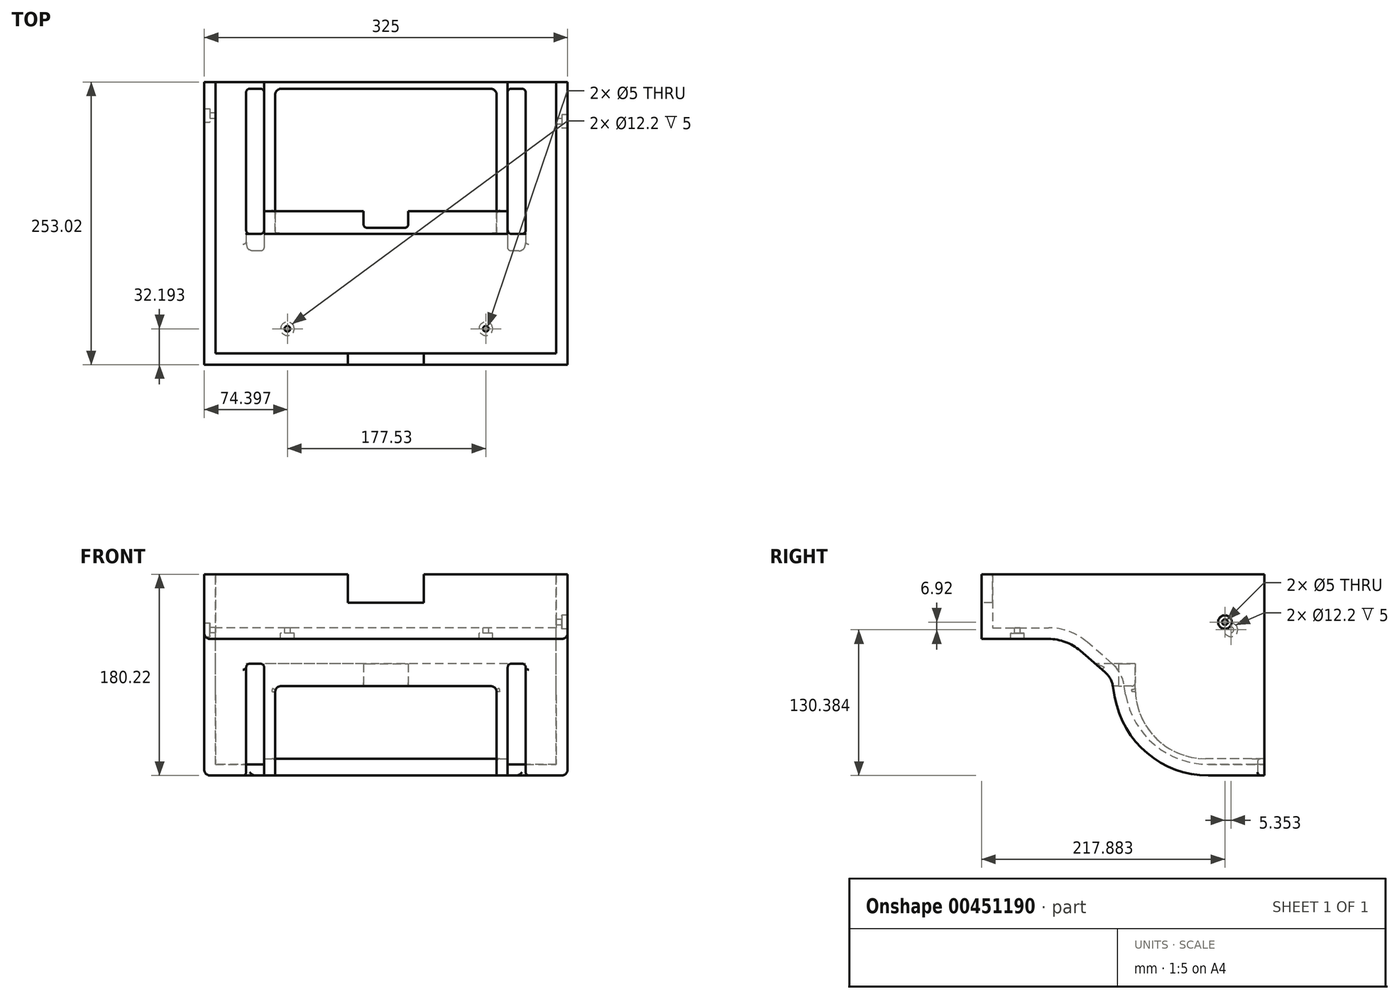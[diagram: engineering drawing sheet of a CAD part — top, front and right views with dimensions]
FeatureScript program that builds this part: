
annotation { "Feature Type Name" : "Feature", "Feature Type Description" : "" }
export const myFeature = defineFeature(function(context is Context, id is Id, definition is map)
    precondition{}
    {
        {
            var Q0;
            Q0=qCreatedBy(makeId("Right.planeOp"),FACE);
            var sketch = newSketch(context, id + "F0", { "sketchPlane" : qUnion([Q0])});
            skLineSegment(sketch, "E0", {"start": v(-253.02, 122.22) * mm, "end": v(-193.02, 122.22) * mm});
            skLineSegment(sketch, "E1", {"start": v(-50, 0) * mm, "end": v(0, 0) * mm});
            skLineSegment(sketch, "E2", {"start": v(0, 0) * mm, "end": v(0, 180.22) * mm});
            skLineSegment(sketch, "E3", {"start": v(0, 180.22) * mm, "end": v(-253.02, 180.22) * mm});
            skLineSegment(sketch, "E4", {"start": v(-253.02, 180.22) * mm, "end": v(-253.02, 122.22) * mm});
            skArc(sketch, "E5", {"start": v(-133.7, 70.24) * mm, "mid": v(-104.63, 19.89) * mm, "end": v(-50, 0) * mm});
            skLineSegment(sketch, "E6", {"start": v(-133.7, 70.24) * mm, "end": v(-135.44, 80.09) * mm});
            skPoint(sketch, "E7", {"position": v(-142.53, 92.57) * mm});
            skArc(sketch, "E8", {"start": v(-135.44, 80.09) * mm, "mid": v(-137.9, 86.94) * mm, "end": v(-142.53, 92.57) * mm});
            skLineSegment(sketch, "E9", {"start": v(-142.53, 92.57) * mm, "end": v(-164.74, 111.7) * mm});
            skArc(sketch, "E10", {"start": v(-164.74, 111.7) * mm, "mid": v(-177.94, 119.5) * mm, "end": v(-193.02, 122.22) * mm});
            skSolve(sketch);
        }
        {
            var Q0;
            Q0=qSketchRegion(id+"F0",true);
            extrude(context, id + "F1", {"entities" : qUnion([Q0]), "depth" : 325 * mm, "offsetDistance" : 25 * mm, "symmetric" : true});
        }
        {
            var Q0;
            Q0=qCreatedBy(makeId("Top.planeOp"),FACE);
            var sketch = newSketch(context, id + "F2", { "sketchPlane" : qUnion([Q0])});
            skLineSegment(sketch, "E11.bottom", {"start": v(-125, -6) * mm, "end": v(-109, -6) * mm});
            skLineSegment(sketch, "E11.top", {"start": v(-125, -161) * mm, "end": v(-109, -161) * mm});
            skLineSegment(sketch, "E11.left", {"start": v(-125, -6) * mm, "end": v(-125, -161) * mm});
            skLineSegment(sketch, "E11.right", {"start": v(-109, -6) * mm, "end": v(-109, -161) * mm});
            skLineSegment(sketch, "E12.MirrorCS", {"start": v(125, -161) * mm, "end": v(109, -161) * mm});
            skLineSegment(sketch, "E13.MirrorCS", {"start": v(125, -6) * mm, "end": v(109, -6) * mm});
            skLineSegment(sketch, "E14.MirrorCS", {"start": v(125, -6) * mm, "end": v(125, -161) * mm});
            skLineSegment(sketch, "E15.MirrorCS", {"start": v(109, -6) * mm, "end": v(109, -161) * mm});
            skLineSegment(sketch, "E16.bottom", {"start": v(99, -6) * mm, "end": v(-99, -6) * mm, "construction": true});
            skLineSegment(sketch, "E16.top", {"start": v(99, -161) * mm, "end": v(-99, -161) * mm, "construction": true});
            skLineSegment(sketch, "E16.left", {"start": v(99, -6) * mm, "end": v(99, -161) * mm, "construction": true});
            skLineSegment(sketch, "E16.right", {"start": v(-99, -6) * mm, "end": v(-99, -161) * mm, "construction": true});
            skPoint(sketch, "E16.middle", {"position": v(0, -83.5) * mm});
            skSolve(sketch);
        }
        {
            var Q0;
            Q0=qSketchRegion(id+"F2",true);
            extrude(context, id + "F3", {"entities" : qUnion([Q0]), "operationType" : NewBodyOperationType.REMOVE, "depth" : 100 * mm, "offsetDistance" : 25 * mm});
        }
        {
            var Q0;
            Q0=makeQuery(id+"F1.opExtrude","SWEPT_FACE",FACE,{"disambiguationData":[OSD([sQuery(id+"F0.wireOp",EDGE,"E2")])]});
            var Q1;
            Q1=makeQuery(id+"F3.boolean.opBoolean","COPY",FACE,{"derivedFrom":makeQuery(id+"F3.opExtrude","SWEPT_FACE",FACE,{"disambiguationData":[OSD([sQuery(id+"F2.wireOp",EDGE,"E11.left")])]})});
            var Q2;
            Q2=makeQuery(id+"F3.boolean.opBoolean","COPY",FACE,{"derivedFrom":makeQuery(id+"F3.opExtrude","SWEPT_FACE",FACE,{"disambiguationData":[OSD([sQuery(id+"F2.wireOp",EDGE,"E14.MirrorCS")])]})});
            var Q3;
            Q3=makeQuery(id+"F3.boolean.opBoolean","COPY",FACE,{"derivedFrom":makeQuery(id+"F3.opExtrude","CAP_FACE",FACE,{"disambiguationData":[OSD([sQuery(id+"F2.wireOp",EDGE,"E12.MirrorCS"),sQuery(id+"F2.wireOp",EDGE,"E13.MirrorCS"),sQuery(id+"F2.wireOp",EDGE,"E14.MirrorCS"),sQuery(id+"F2.wireOp",EDGE,"E15.MirrorCS")])],"isStart":false})});
            var Q4;
            Q4=makeQuery(id+"F3.boolean.opBoolean","COPY",FACE,{"derivedFrom":makeQuery(id+"F3.opExtrude","CAP_FACE",FACE,{"disambiguationData":[OSD([sQuery(id+"F2.wireOp",EDGE,"E11.bottom"),sQuery(id+"F2.wireOp",EDGE,"E11.top"),sQuery(id+"F2.wireOp",EDGE,"E11.left"),sQuery(id+"F2.wireOp",EDGE,"E11.right")])],"isStart":false})});
            var Q5;
            Q5=makeQuery(id+"F3.boolean.opBoolean","COPY",FACE,{"derivedFrom":makeQuery(id+"F3.opExtrude","SWEPT_FACE",FACE,{"disambiguationData":[OSD([sQuery(id+"F2.wireOp",EDGE,"E11.bottom")])]})});
            var Q6;
            Q6=makeQuery(id+"F3.boolean.opBoolean","COPY",FACE,{"derivedFrom":makeQuery(id+"F3.opExtrude","SWEPT_FACE",FACE,{"disambiguationData":[OSD([sQuery(id+"F2.wireOp",EDGE,"E13.MirrorCS")])]})});
            var Q7;
            Q7=makeQuery(id+"F1.opExtrude","SWEPT_FACE",FACE,{"disambiguationData":[OSD([sQuery(id+"F0.wireOp",EDGE,"E3")])]});
            shell(context, id + "F4", {"entities" : qUnion([Q0, Q1, Q2, Q3, Q4, Q5, Q6, Q7]), "thickness" : 10 * mm});
        }
        {
            var Q0;
            Q0=makeQuery(id+"F4.opShell","OFFSET_FACE",FACE,{"disambiguationData":[OSD([sQuery(id+"F2.wireOp",EDGE,"E11.right")])]});
            extrude(context, id + "F5", {"entities" : qUnion([Q0]), "operationType" : NewBodyOperationType.ADD, "depth" : 200 * mm, "offsetDistance" : 25 * mm});
        }
        {
            var Q0;
            {var subQ0=sQuery(id+"F2.wireOp",EDGE,"E11.bottom");Q0=makeQuery(id+"F5.boolean.opBoolean","MERGE",FACE,{"derivedFrom":[makeQuery(id+"F4.opShell","OFFSET_FACE",FACE,{"disambiguationData":[OSD([subQ0])]}),makeQuery(id+"F4.opShell","OFFSET_FACE",FACE,{"disambiguationData":[OSD([sQuery(id+"F2.wireOp",EDGE,"E13.MirrorCS")])]}),makeQuery(id+"F5.opExtrude","SWEPT_FACE",FACE,{"disambiguationData":[OSD([subQ0,sQuery(id+"F2.wireOp",EDGE,"E11.right")])]})]});}
            extrude(context, id + "F6", {"entities" : qUnion([Q0]), "operationType" : NewBodyOperationType.ADD, "depth" : 6 * mm, "offsetDistance" : 25 * mm});
        }
        {
            var Q0;
            Q0=makeQuery(id+"F1.opExtrude","SWEPT_FACE",FACE,{"disambiguationData":[OSD([sQuery(id+"F0.wireOp",EDGE,"E1")])]});
            var sketch = newSketch(context, id + "F7", { "sketchPlane" : qUnion([Q0])});
            skLineSegment(sketch, "E17.bottom", {"start": v(99, 5.98) * mm, "end": v(-99, 5.98) * mm});
            skLineSegment(sketch, "E17.top", {"start": v(99, 171.27) * mm, "end": v(-99, 171.27) * mm});
            skLineSegment(sketch, "E17.left", {"start": v(99, 5.98) * mm, "end": v(99, 171.27) * mm});
            skLineSegment(sketch, "E17.right", {"start": v(-99, 5.98) * mm, "end": v(-99, 171.27) * mm});
            skPoint(sketch, "E17.middle", {"position": v(0, 88.63) * mm});
            skSolve(sketch);
        }
        {
            var Q0;
            Q0=qSketchRegion(id+"F7",true);
            extrude(context, id + "F8", {"entities" : qUnion([Q0]), "operationType" : NewBodyOperationType.REMOVE, "oppositeDirection" : true, "depth" : 80 * mm, "offsetDistance" : 25 * mm});
        }
        {
            var Q0;
            Q0=qCreatedBy(makeId("Right.planeOp"),FACE);
            var sketch = newSketch(context, id + "F9", { "sketchPlane" : qUnion([Q0])});
            skLineSegment(sketch, "E18.0", {"start": v(-5.98, 80) * mm, "end": v(-135.42, 80) * mm, "construction": true});
            skArc(sketch, "E18.1", {"start": v(-133.7, 70.24) * mm, "mid": v(-104.63, 19.89) * mm, "end": v(-50, 0) * mm, "construction": true});
            skLineSegment(sketch, "E18.2", {"start": v(-133.7, 70.24) * mm, "end": v(-135.42, 80) * mm, "construction": true});
            skLineSegment(sketch, "E18.3", {"start": v(-5.98, 0) * mm, "end": v(-50, 0) * mm, "construction": true});
            skLineSegment(sketch, "E18.4", {"start": v(-5.98, 80) * mm, "end": v(-5.98, 0) * mm, "construction": true});
            skLineSegment(sketch, "E19", {"start": v(-135.42, 80) * mm, "end": v(-135.42, 80) * mm});
            skPoint(sketch, "E20", {"position": v(-5.98, 32.45) * mm});
            skLineSegment(sketch, "E21", {"start": v(-115.42, 78) * mm, "end": v(-115.42, 80) * mm});
            skLineSegment(sketch, "E22", {"start": v(-5.98, 15) * mm, "end": v(-52.42, 15) * mm});
            skArc(sketch, "E23", {"start": v(-115.42, 78) * mm, "mid": v(-96.97, 33.45) * mm, "end": v(-52.42, 15) * mm});
            skLineSegment(sketch, "E24", {"start": v(-115.42, 80) * mm, "end": v(-115.42, 125.47) * mm});
            skLineSegment(sketch, "E25", {"start": v(-5.98, 15) * mm, "end": v(10.68, 15) * mm});
            skLineSegment(sketch, "E26", {"start": v(10.68, 15) * mm, "end": v(10.68, 125.47) * mm});
            skLineSegment(sketch, "E27", {"start": v(10.68, 125.47) * mm, "end": v(-115.42, 125.47) * mm});
            skSolve(sketch);
        }
        {
            var Q0;
            Q0=qSketchRegion(id+"F9",true);
            extrude(context, id + "F10", {"entities" : qUnion([Q0]), "operationType" : NewBodyOperationType.REMOVE, "oppositeDirection" : true, "depth" : 232 * mm, "offsetDistance" : 25 * mm, "symmetric" : true});
        }
        {
            var Q0;
            Q0=makeQuery(id+"F8.boolean.opBoolean","COPY",FACE,{"derivedFrom":makeQuery(id+"F8.opExtrude","CAP_FACE",FACE,{"disambiguationData":[OSD([sQuery(id+"F7.wireOp",EDGE,"E17.bottom"),sQuery(id+"F7.wireOp",EDGE,"E17.top"),sQuery(id+"F7.wireOp",EDGE,"E17.left"),sQuery(id+"F7.wireOp",EDGE,"E17.right")])],"isStart":false})});
            var sketch = newSketch(context, id + "F11", { "sketchPlane" : qUnion([Q0])});
            skLineSegment(sketch, "E28.bottom", {"start": v(20, 115.42) * mm, "end": v(-20, 115.42) * mm});
            skLineSegment(sketch, "E28.top", {"start": v(20, 130.42) * mm, "end": v(-20, 130.42) * mm});
            skLineSegment(sketch, "E28.left", {"start": v(20, 115.42) * mm, "end": v(20, 130.42) * mm});
            skLineSegment(sketch, "E28.right", {"start": v(-20, 115.42) * mm, "end": v(-20, 130.42) * mm});
            skPoint(sketch, "E28.middle", {"position": v(0, 122.92) * mm});
            skSolve(sketch);
        }
        {
            var Q0;
            Q0=qSketchRegion(id+"F11",true);
            extrude(context, id + "F12", {"entities" : qUnion([Q0]), "operationType" : NewBodyOperationType.REMOVE, "oppositeDirection" : true, "depth" : 25 * mm, "offsetDistance" : 25 * mm});
        }
        {
            var Q0;
            Q0=makeQuery(id+"F3.boolean.opBoolean","COPY",EDGE,{"derivedFrom":makeQuery(id+"F3.opExtrude","SWEPT_EDGE",EDGE,{"disambiguationData":[OSD([sQuery(id+"F2.wireOp",EDGE,"E11.bottom"),sQuery(id+"F2.wireOp",EDGE,"E11.left")])]})});
            var Q1;
            Q1=makeQuery(id+"F4.opShell","OFFSET_EDGE",EDGE,{"disambiguationData":[OSD([sQuery(id+"F2.wireOp",EDGE,"E11.bottom"),sQuery(id+"F2.wireOp",EDGE,"E11.right")]),OD(0.0)]});
            var Q2;
            {var subQ0=sQuery(id+"F2.wireOp",EDGE,"E15.MirrorCS");Q2=makeQuery(id+"F4.opShell","OFFSET_EDGE",EDGE,{"disambiguationData":[OSD([subQ0]),TDD([makeQuery(id+"F3.boolean.opBoolean","COPY",EDGE,{"derivedFrom":makeQuery(id+"F3.opExtrude","CAP_EDGE",EDGE,{"disambiguationData":[OSD([subQ0])],"isStart":false})})]),OD(0.0)]});}
            var Q3;
            Q3=makeQuery(id+"F3.boolean.opBoolean","COPY",EDGE,{"derivedFrom":makeQuery(id+"F3.opExtrude","SWEPT_EDGE",EDGE,{"disambiguationData":[OSD([sQuery(id+"F2.wireOp",EDGE,"E13.MirrorCS"),sQuery(id+"F2.wireOp",EDGE,"E14.MirrorCS")])]})});
            var Q4;
            Q4=makeQuery(id+"F4.opShell","OFFSET_EDGE",EDGE,{"disambiguationData":[OSD([sQuery(id+"F2.wireOp",EDGE,"E13.MirrorCS"),sQuery(id+"F2.wireOp",EDGE,"E15.MirrorCS")]),OD(0.0)]});
            var Q5;
            Q5=makeQuery(id+"F12.boolean.opBoolean","COPY",EDGE,{"derivedFrom":makeQuery(id+"F12.opExtrude","SWEPT_EDGE",EDGE,{"disambiguationData":[OSD([sQuery(id+"F7.wireOp",EDGE,"E17.bottom"),sQuery(id+"F7.wireOp",EDGE,"E17.top"),sQuery(id+"F7.wireOp",EDGE,"E17.left"),sQuery(id+"F7.wireOp",EDGE,"E17.right"),sQuery(id+"F9.wireOp",EDGE,"E21"),sQuery(id+"F9.wireOp",EDGE,"E24"),sQuery(id+"F11.wireOp",EDGE,"E28.bottom"),sQuery(id+"F11.wireOp",EDGE,"E28.right")])]})});
            var Q6;
            Q6=makeQuery(id+"F12.boolean.opBoolean","COPY",EDGE,{"derivedFrom":makeQuery(id+"F12.opExtrude","SWEPT_EDGE",EDGE,{"disambiguationData":[OSD([sQuery(id+"F11.wireOp",EDGE,"E28.top"),sQuery(id+"F11.wireOp",EDGE,"E28.right")])]})});
            var Q7;
            Q7=makeQuery(id+"F12.boolean.opBoolean","COPY",EDGE,{"derivedFrom":makeQuery(id+"F12.opExtrude","SWEPT_EDGE",EDGE,{"disambiguationData":[OSD([sQuery(id+"F11.wireOp",EDGE,"E28.top"),sQuery(id+"F11.wireOp",EDGE,"E28.left")])]})});
            var Q8;
            Q8=makeQuery(id+"F12.boolean.opBoolean","COPY",EDGE,{"derivedFrom":makeQuery(id+"F12.opExtrude","SWEPT_EDGE",EDGE,{"disambiguationData":[OSD([sQuery(id+"F7.wireOp",EDGE,"E17.bottom"),sQuery(id+"F7.wireOp",EDGE,"E17.top"),sQuery(id+"F7.wireOp",EDGE,"E17.left"),sQuery(id+"F7.wireOp",EDGE,"E17.right"),sQuery(id+"F9.wireOp",EDGE,"E21"),sQuery(id+"F9.wireOp",EDGE,"E24"),sQuery(id+"F11.wireOp",EDGE,"E28.bottom"),sQuery(id+"F11.wireOp",EDGE,"E28.left")])]})});
            var Q9;
            {var subQ0=sQuery(id+"F2.wireOp",EDGE,"E11.right");Q9=makeQuery(id+"F4.opShell","OFFSET_EDGE",EDGE,{"disambiguationData":[OSD([subQ0]),TDD([makeQuery(id+"F3.boolean.opBoolean","COPY",EDGE,{"derivedFrom":makeQuery(id+"F3.opExtrude","CAP_EDGE",EDGE,{"disambiguationData":[OSD([subQ0])],"isStart":false})})]),OD(0.0)]});}
            var Q10;
            Q10=makeQuery(id+"F3.boolean.opBoolean","INTERSECT",EDGE,{"derivedFrom":[makeQuery(id+"F1.opExtrude","SWEPT_FACE",FACE,{"disambiguationData":[OSD([sQuery(id+"F0.wireOp",EDGE,"E5")])]}),makeQuery(id+"F3.opExtrude","SWEPT_FACE",FACE,{"disambiguationData":[OSD([sQuery(id+"F2.wireOp",EDGE,"E11.left")])]})]});
            var Q11;
            Q11=makeQuery(id+"F3.boolean.opBoolean","INTERSECT",EDGE,{"derivedFrom":[makeQuery(id+"F1.opExtrude","SWEPT_FACE",FACE,{"disambiguationData":[OSD([sQuery(id+"F0.wireOp",EDGE,"E5")])]}),makeQuery(id+"F3.opExtrude","SWEPT_FACE",FACE,{"disambiguationData":[OSD([sQuery(id+"F2.wireOp",EDGE,"E14.MirrorCS")])]})]});
            var Q12;
            {var subQ0=sQuery(id+"F2.wireOp",EDGE,"E11.left");Q12=makeQuery(id+"F4.opShell","OFFSET_EDGE",EDGE,{"disambiguationData":[OSD([subQ0]),TDD([makeQuery(id+"F3.boolean.opBoolean","COPY",EDGE,{"derivedFrom":makeQuery(id+"F3.opExtrude","CAP_EDGE",EDGE,{"disambiguationData":[OSD([subQ0])],"isStart":false})})])]});}
            var Q13;
            {var subQ0=sQuery(id+"F2.wireOp",EDGE,"E14.MirrorCS");Q13=makeQuery(id+"F4.opShell","OFFSET_EDGE",EDGE,{"disambiguationData":[OSD([subQ0]),TDD([makeQuery(id+"F3.boolean.opBoolean","COPY",EDGE,{"derivedFrom":makeQuery(id+"F3.opExtrude","CAP_EDGE",EDGE,{"disambiguationData":[OSD([subQ0])],"isStart":false})})])]});}
            fillet(context, id + "F13", {"entities" : qUnion([Q0, Q1, Q2, Q3, Q4, Q5, Q6, Q7, Q8, Q9, Q10, Q11, Q12, Q13]), "radius" : 3 * mm, "tangentPropagation" : true, "allowEdgeOverflow" : false});
        }
        {
            var Q0;
            Q0=makeQuery(id+"F8.boolean.opBoolean","COPY",EDGE,{"derivedFrom":makeQuery(id+"F8.opExtrude","SWEPT_EDGE",EDGE,{"disambiguationData":[OSD([sQuery(id+"F7.wireOp",EDGE,"E17.bottom"),sQuery(id+"F7.wireOp",EDGE,"E17.right")])]})});
            var Q1;
            Q1=makeQuery(id+"F8.boolean.opBoolean","COPY",EDGE,{"derivedFrom":makeQuery(id+"F8.opExtrude","SWEPT_EDGE",EDGE,{"disambiguationData":[OSD([sQuery(id+"F7.wireOp",EDGE,"E17.bottom"),sQuery(id+"F7.wireOp",EDGE,"E17.left")])]})});
            var Q2;
            Q2=makeQuery(id+"F8.boolean.opBoolean","COPY",EDGE,{"derivedFrom":makeQuery(id+"F8.opExtrude","CAP_EDGE",EDGE,{"disambiguationData":[OSD([sQuery(id+"F7.wireOp",EDGE,"E17.left")])],"isStart":false})});
            var Q3;
            Q3=makeQuery(id+"F8.boolean.opBoolean","COPY",EDGE,{"derivedFrom":makeQuery(id+"F8.opExtrude","CAP_EDGE",EDGE,{"disambiguationData":[OSD([sQuery(id+"F7.wireOp",EDGE,"E17.right")])],"isStart":false})});
            fillet(context, id + "F14", {"entities" : qUnion([Q0, Q1, Q2, Q3]), "radius" : 5 * mm, "tangentPropagation" : true, "allowEdgeOverflow" : false});
        }
        {
            var Q0;
            Q0=makeQuery(id+"F8.boolean.opBoolean","INTERSECT",EDGE,{"derivedFrom":[makeQuery(id+"F1.opExtrude","SWEPT_FACE",FACE,{"disambiguationData":[OSD([sQuery(id+"F0.wireOp",EDGE,"08491e43-bc0c-4947-b1fe-aeb562bb6d01")])]}),makeQuery(id+"F8.opExtrude","CAP_FACE",FACE,{"disambiguationData":[OSD([sQuery(id+"F7.wireOp",EDGE,"E17.bottom"),sQuery(id+"F7.wireOp",EDGE,"E17.top"),sQuery(id+"F7.wireOp",EDGE,"E17.left"),sQuery(id+"F7.wireOp",EDGE,"E17.right")])],"isStart":false})]});
            var Q1;
            {var subQ0=sQuery(id+"F7.wireOp",EDGE,"E17.right");var subQ1=makeQuery(id+"F8.boolean.opBoolean","COPY",FACE,{"derivedFrom":makeQuery(id+"F8.opExtrude","CAP_FACE",FACE,{"disambiguationData":[OSD([sQuery(id+"F7.wireOp",EDGE,"E17.bottom"),sQuery(id+"F7.wireOp",EDGE,"E17.top"),sQuery(id+"F7.wireOp",EDGE,"E17.left"),subQ0])],"isStart":false})});var subQ2=makeQuery(id+"F10.opExtrude","SWEPT_FACE",FACE,{"disambiguationData":[OSD([sQuery(id+"F9.wireOp",EDGE,"E21"),sQuery(id+"F9.wireOp",EDGE,"E24")])]});Q1=makeQuery(id+"F12.boolean.opBoolean","SPLIT",EDGE,{"disambiguationData":[TD([makeQuery(id+"F8.boolean.opBoolean","COPY",FACE,{"derivedFrom":makeQuery(id+"F8.opExtrude","SWEPT_FACE",FACE,{"disambiguationData":[OSD([subQ0])]})})])],"derivedFrom":makeQuery(id+"F10.boolean.opBoolean","INTERSECT",EDGE,{"derivedFrom":[subQ1,subQ2]})});}
            fillet(context, id + "F15", {"entities" : qUnion([Q0, Q1]), "radius" : 3 * mm, "tangentPropagation" : true, "allowEdgeOverflow" : false});
        }
        {
            var Q0;
            Q0=makeQuery(id+"F1.opExtrude","CAP_EDGE",EDGE,{"disambiguationData":[OSD([sQuery(id+"F0.wireOp",EDGE,"E5")])],"isStart":true});
            var Q1;
            Q1=makeQuery(id+"F1.opExtrude","CAP_EDGE",EDGE,{"disambiguationData":[OSD([sQuery(id+"F0.wireOp",EDGE,"E5")])],"isStart":false});
            fillet(context, id + "F16", {"entities" : qUnion([Q0, Q1]), "radius" : 5 * mm, "tangentPropagation" : true, "allowEdgeOverflow" : false});
        }
        {
            var Q0;
            Q0=makeQuery(id+"F1.opExtrude","SWEPT_FACE",FACE,{"disambiguationData":[OSD([sQuery(id+"F0.wireOp",EDGE,"E4")])]});
            var sketch = newSketch(context, id + "F17", { "sketchPlane" : qUnion([Q0])});
            skLineSegment(sketch, "E29.bottom", {"start": v(34, 180.22) * mm, "end": v(-34, 180.22) * mm});
            skLineSegment(sketch, "E29.top", {"start": v(34, 154.8) * mm, "end": v(-34, 154.8) * mm});
            skLineSegment(sketch, "E29.left", {"start": v(34, 180.22) * mm, "end": v(34, 154.8) * mm});
            skLineSegment(sketch, "E29.right", {"start": v(-34, 180.22) * mm, "end": v(-34, 154.8) * mm});
            skPoint(sketch, "E29.middle", {"position": v(0, 167.51) * mm});
            skPoint(sketch, "E29.middle.positionSnap0", {"position": v(0, 180.22) * mm});
            skPoint(sketch, "E29.centerSnap0", {"position": v(0, 180.22) * mm});
            skSolve(sketch);
        }
        {
            var Q0;
            Q0=qSketchRegion(id+"F17",true);
            extrude(context, id + "F18", {"entities" : qUnion([Q0]), "operationType" : NewBodyOperationType.REMOVE, "oppositeDirection" : true, "depth" : 25 * mm, "offsetDistance" : 25 * mm});
        }
        {
            var Q0;
            Q0=makeQuery(id+"F1.opExtrude","SWEPT_FACE",FACE,{"disambiguationData":[OSD([sQuery(id+"F0.wireOp",EDGE,"E0")])]});
            var sketch = newSketch(context, id + "F19", { "sketchPlane" : qUnion([Q0])});
            skPoint(sketch, "E30", {"position": v(-88.1, 220.83) * mm});
            skPoint(sketch, "E31", {"position": v(89.43, 220.83) * mm});
            skSolve(sketch);
        }
        {
            var Q0;
            Q0=makeQuery(id+"F1.opExtrude","CAP_FACE",FACE,{"disambiguationData":[OSD([sQuery(id+"F0.wireOp",EDGE,"E0"),sQuery(id+"F0.wireOp",EDGE,"E1"),sQuery(id+"F0.wireOp",EDGE,"E2"),sQuery(id+"F0.wireOp",EDGE,"E3"),sQuery(id+"F0.wireOp",EDGE,"E4"),sQuery(id+"F0.wireOp",EDGE,"E5"),sQuery(id+"F0.wireOp",EDGE,"E6"),sQuery(id+"F0.wireOp",EDGE,"08491e43-bc0c-4947-b1fe-aeb562bb6d01")])],"isStart":false});
            var sketch = newSketch(context, id + "F20", { "sketchPlane" : qUnion([Q0])});
            skPoint(sketch, "E32", {"position": v(-35.14, 137.3) * mm});
            skSolve(sketch);
        }
        {
            var Q0;
            Q0=makeQuery(id+"F1.opExtrude","CAP_FACE",FACE,{"disambiguationData":[OSD([sQuery(id+"F0.wireOp",EDGE,"E0"),sQuery(id+"F0.wireOp",EDGE,"E1"),sQuery(id+"F0.wireOp",EDGE,"E2"),sQuery(id+"F0.wireOp",EDGE,"E3"),sQuery(id+"F0.wireOp",EDGE,"E4"),sQuery(id+"F0.wireOp",EDGE,"E5"),sQuery(id+"F0.wireOp",EDGE,"E6"),sQuery(id+"F0.wireOp",EDGE,"08491e43-bc0c-4947-b1fe-aeb562bb6d01")])],"isStart":true});
            var sketch = newSketch(context, id + "F21", { "sketchPlane" : qUnion([Q0])});
            skPoint(sketch, "E33", {"position": v(29.78, 130.38) * mm});
            skSolve(sketch);
        }
        {
            var Q0;
            Q0=sQuery(id+"F19.wireOp",VERTEX,"E30");
            var Q1;
            Q1=sQuery(id+"F19.wireOp",VERTEX,"E31");
            var Q2;
            Q2=sQuery(id+"F21.wireOp",VERTEX,"E33");
            var Q3;
            Q3=sQuery(id+"F20.wireOp",VERTEX,"E32");
            var Q4;
            Q4=makeQuery(id+"F1.opExtrude","SWEPT_BODY",BODY,{"disambiguationData":[OSD([sQuery(id+"F0.wireOp",EDGE,"E0"),sQuery(id+"F0.wireOp",EDGE,"E1"),sQuery(id+"F0.wireOp",EDGE,"E2"),sQuery(id+"F0.wireOp",EDGE,"E3"),sQuery(id+"F0.wireOp",EDGE,"E4"),sQuery(id+"F0.wireOp",EDGE,"E5"),sQuery(id+"F0.wireOp",EDGE,"E6"),sQuery(id+"F0.wireOp",EDGE,"08491e43-bc0c-4947-b1fe-aeb562bb6d01")])]});
            hole(context, id + "F22", {"style" : HoleStyle.C_BORE, "endStyle" : HoleEndStyle.BLIND, "holeDiameter" : 5 * mm, "cBoreDiameter" : 12.2 * mm, "cBoreDepth" : 5 * mm, "majorDiameter" : 5 * mm, "holeDepth" : 10 * mm, "tappedDepth" : 12 * mm, "tapClearance" : 3, "locations" : qUnion([Q0, Q1, Q2, Q3]), "scope" : qUnion([Q4])});
        }
    });
